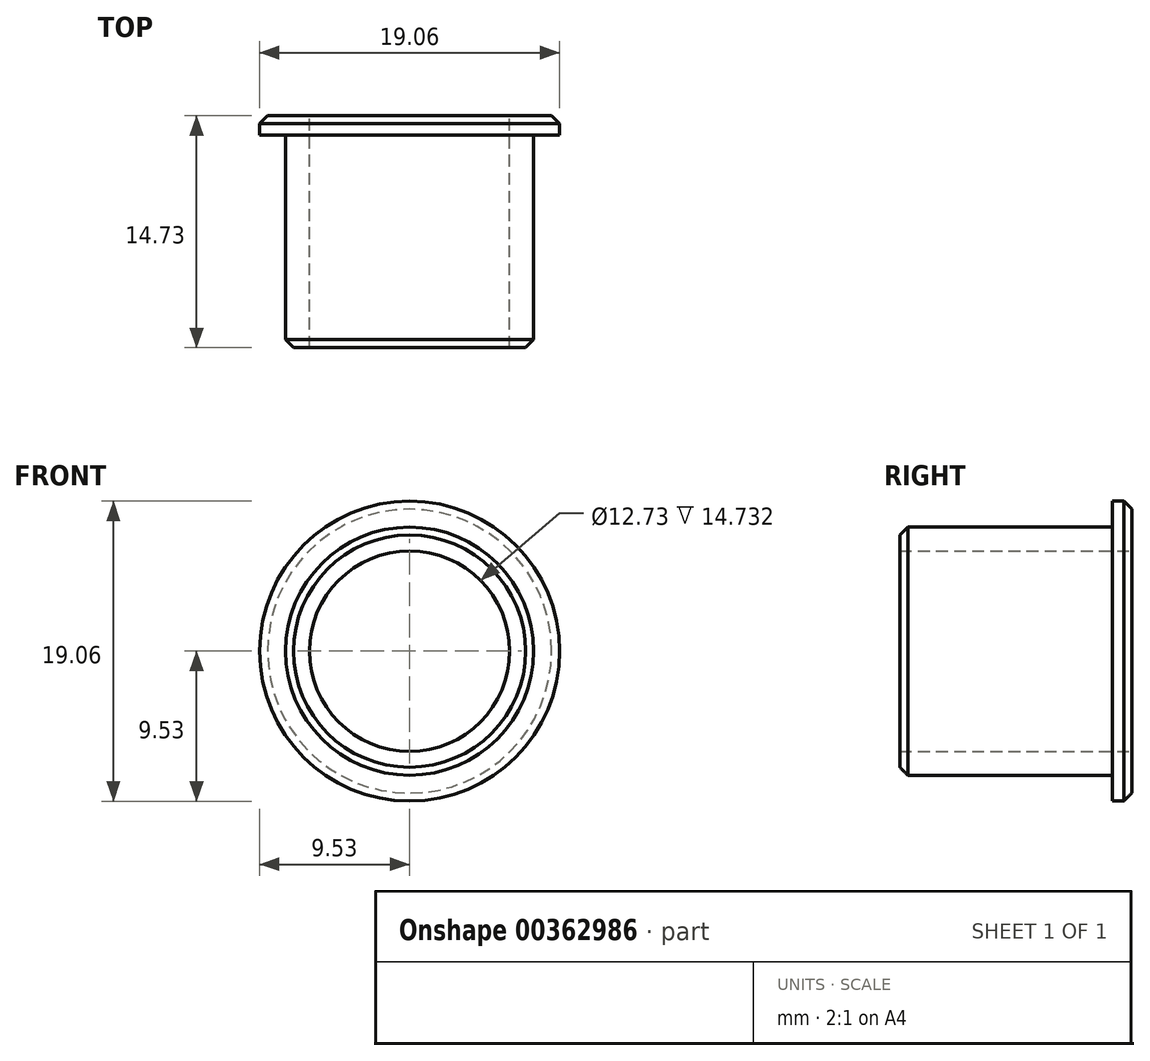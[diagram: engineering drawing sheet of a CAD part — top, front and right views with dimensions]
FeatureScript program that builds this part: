
annotation { "Feature Type Name" : "Feature", "Feature Type Description" : "" }
export const myFeature = defineFeature(function(context is Context, id is Id, definition is map)
    precondition{}
    {
        {
            var Q0;
            Q0=qCreatedBy(makeId("Front.planeOp"),FACE);
            var sketch = newSketch(context, id + "F0", { "sketchPlane" : qUnion([Q0])});
            skCircle(sketch, "E0", {"center": v(0, 0) * mm, "radius": 9.53 * mm});
            skCircle(sketch, "E1", {"center": v(0, 0) * mm, "radius": 6.36 * mm});
            skSolve(sketch);
        }
        {
            var Q0;
            Q0=makeQuery(id+"F0.imprint","IMPRINT",FACE,{"disambiguationData":[TD([[makeQuery(id+"F0.imprint","IMPRINT",EDGE,{"derivedFrom":sQuery(id+"F0.wireOp",EDGE,"E0")}),1.0]])]});
            extrude(context, id + "F1", {"entities" : qUnion([Q0]), "depth" : 1.22 * mm});
        }
        {
            var Q0;
            Q0=makeQuery(id+"F1.opExtrude","CAP_FACE",FACE,{"disambiguationData":[OSD([sQuery(id+"F0.wireOp",EDGE,"E0"),sQuery(id+"F0.wireOp",EDGE,"E1")])],"isStart":false});
            var sketch = newSketch(context, id + "F2", { "sketchPlane" : qUnion([Q0])});
            skCircle(sketch, "E2", {"center": v(0, 0) * mm, "radius": 7.88 * mm});
            skSolve(sketch);
        }
        {
            var Q0;
            Q0=makeQuery(id+"F2.imprint","IMPRINT",FACE,{"disambiguationData":[TD([[makeQuery(id+"F2.imprint","IMPRINT",EDGE,{"derivedFrom":sQuery(id+"F2.wireOp",EDGE,"E2")}),1.0]])]});
            extrude(context, id + "F3", {"entities" : qUnion([Q0]), "operationType" : NewBodyOperationType.ADD, "depth" : 13.5 * mm});
        }
        {
            var Q0;
            Q0=makeQuery(id+"F1.opExtrude","CAP_EDGE",EDGE,{"disambiguationData":[OSD([sQuery(id+"F0.wireOp",EDGE,"E0")])],"isStart":true});
            var Q1;
            Q1=makeQuery(id+"F3.opExtrude","CAP_EDGE",EDGE,{"disambiguationData":[OSD([sQuery(id+"F2.wireOp",EDGE,"E2")])],"isStart":false});
            chamfer(context, id + "F4", {"entities" : qUnion([Q0, Q1]), "chamferType" : ChamferType.OFFSET_ANGLE, "width" : 0.5 * mm, "oppositeDirection" : false, "angle" : 45 * degree, "tangentPropagation" : true});
        }
    });
